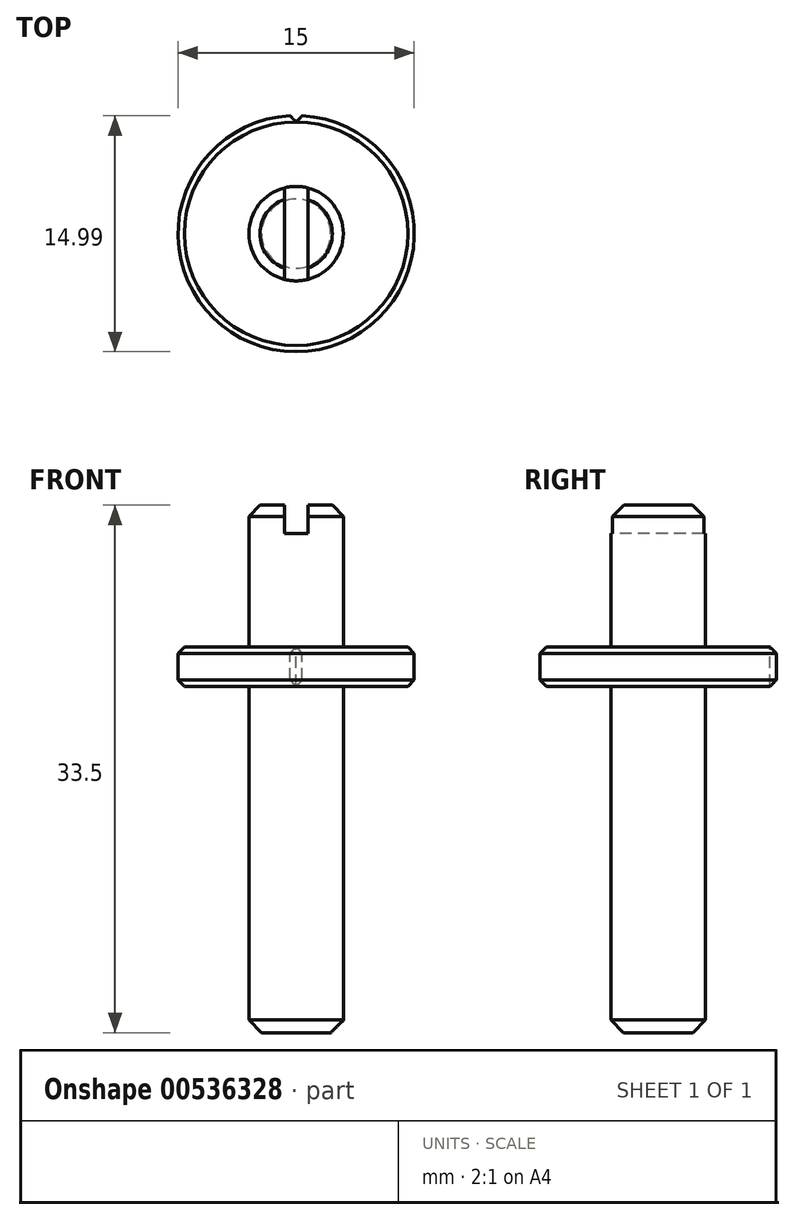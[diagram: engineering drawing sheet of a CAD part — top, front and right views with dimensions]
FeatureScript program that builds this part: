
annotation { "Feature Type Name" : "Feature", "Feature Type Description" : "" }
export const myFeature = defineFeature(function(context is Context, id is Id, definition is map)
    precondition{}
    {
        {
            var Q0;
            Q0=qCreatedBy(makeId("Front.planeOp"),FACE);
            var sketch = newSketch(context, id + "F0", { "sketchPlane" : qUnion([Q0])});
            skLineSegment(sketch, "E0", {"start": v(0, 9) * mm, "end": v(0, -24.5) * mm});
            skLineSegment(sketch, "E1", {"start": v(0, 9) * mm, "end": v(3, 9) * mm});
            skLineSegment(sketch, "E2", {"start": v(3, 9) * mm, "end": v(3, 0) * mm});
            skLineSegment(sketch, "E3", {"start": v(3, 0) * mm, "end": v(7.5, 0) * mm});
            skLineSegment(sketch, "E4", {"start": v(7.5, 0) * mm, "end": v(7.5, -2.5) * mm});
            skLineSegment(sketch, "E5", {"start": v(7.5, -2.5) * mm, "end": v(3, -2.5) * mm});
            skLineSegment(sketch, "E6", {"start": v(3, -2.5) * mm, "end": v(3, -24.5) * mm});
            skLineSegment(sketch, "E7", {"start": v(3, -24.5) * mm, "end": v(0, -24.5) * mm});
            skLineSegment(sketch, "E8", {"start": v(0, 9) * mm, "end": v(0, 17.77) * mm, "construction": true});
            skSolve(sketch);
        }
        {
            var Q0;
            Q0 = qSketchRegion(id + "F0", true);
            var Q1;
            Q1=sQuery(id+"F0.wireOp",EDGE,"E8");
            revolve(context, id + "F1", {"entities" : qUnion([Q0]), "axis" : qUnion([Q1]), "revolveType" : RevolveType.FULL});
        }
        {
            var Q0;
            Q0=makeQuery(id+"F1.opRevolve","SWEPT_EDGE",EDGE,{"disambiguationData":[OSD([sQuery(id+"F0.wireOp",EDGE,"E6"),sQuery(id+"F0.wireOp",EDGE,"E7")])]});
            chamfer(context, id + "F2", {"entities" : qUnion([Q0]), "width" : .8 * mm, "tangentPropagation" : true});
        }
        {
            var Q0;
            Q0=makeQuery(id+"F1.opRevolve","SWEPT_EDGE",EDGE,{"disambiguationData":[OSD([sQuery(id+"F0.wireOp",EDGE,"E1"),sQuery(id+"F0.wireOp",EDGE,"E2")])]});
            chamfer(context, id + "F3", {"entities" : qUnion([Q0]), "width" : .7 * mm, "tangentPropagation" : true});
        }
        {
            var Q0;
            Q0=makeQuery(id+"F1.opRevolve","SWEPT_EDGE",EDGE,{"disambiguationData":[OSD([sQuery(id+"F0.wireOp",EDGE,"E4"),sQuery(id+"F0.wireOp",EDGE,"E5")])]});
            var Q1;
            Q1=makeQuery(id+"F1.opRevolve","SWEPT_EDGE",EDGE,{"disambiguationData":[OSD([sQuery(id+"F0.wireOp",EDGE,"E3"),sQuery(id+"F0.wireOp",EDGE,"E4")])]});
            chamfer(context, id + "F4", {"entities" : qUnion([Q0, Q1]), "width" : .4 * mm, "tangentPropagation" : true});
        }
        {
            var Q0;
            Q0=qCreatedBy(makeId("Front.planeOp"),FACE);
            var sketch = newSketch(context, id + "F5", { "sketchPlane" : qUnion([Q0])});
            skLineSegment(sketch, "E9.bottom", {"start": v(0.75, 9) * mm, "end": v(-0.75, 9) * mm});
            skLineSegment(sketch, "E9.top", {"start": v(0.75, 7.2) * mm, "end": v(-0.75, 7.2) * mm});
            skLineSegment(sketch, "E9.left", {"start": v(0.75, 9) * mm, "end": v(0.75, 7.2) * mm});
            skLineSegment(sketch, "E9.right", {"start": v(-0.75, 9) * mm, "end": v(-0.75, 7.2) * mm});
            skPoint(sketch, "E9.middle", {"position": v(0, 8.1) * mm});
            skSolve(sketch);
        }
        {
            var Q0;
            Q0 = qSketchRegion(id + "F5", true);
            extrude(context, id + "F6", {"entities" : qUnion([Q0]), "operationType" : NewBodyOperationType.REMOVE, "endBound" : BoundingType.THROUGH_ALL, "oppositeDirection" : true, "depth" : 25 * mm, "offsetDistance" : 25 * mm, "hasSecondDirection" : true, "secondDirectionBound" : SecondDirectionBoundingType.THROUGH_ALL, "secondDirectionOppositeDirection" : false, "secondDirectionDepth" : 25 * mm});
        }
        {
            var Q0;
            Q0=makeQuery(id+"F1.opRevolve","SWEPT_FACE",FACE,{"disambiguationData":[OSD([sQuery(id+"F0.wireOp",EDGE,"E3")])]});
            var sketch = newSketch(context, id + "F7", { "sketchPlane" : qUnion([Q0])});
            skLineSegment(sketch, "E10", {"start": v(0, 0) * mm, "end": v(0, 8.4) * mm, "construction": true});
            skLineSegment(sketch, "E11", {"start": v(0, 7.1) * mm, "end": v(0.39, 7.49) * mm});
            skLineSegment(sketch, "E12", {"start": v(0, 7.1) * mm, "end": v(-0.39, 7.49) * mm});
            skArc(sketch, "E13.0", {"start": v(0.39, 7.49) * mm, "mid": v(0, 7.5) * mm, "end": v(-0.39, 7.49) * mm});
            skSolve(sketch);
        }
        {
            var Q0;
            Q0 = qSketchRegion(id + "F7", true);
            extrude(context, id + "F8", {"entities" : qUnion([Q0]), "operationType" : NewBodyOperationType.REMOVE, "endBound" : BoundingType.THROUGH_ALL, "oppositeDirection" : true, "depth" : 25 * mm, "offsetDistance" : 25 * mm});
        }
    });
